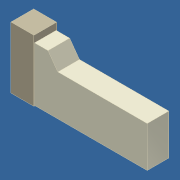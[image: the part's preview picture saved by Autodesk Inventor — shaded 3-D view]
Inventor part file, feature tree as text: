
AUTODESK INVENTOR PART (.ipt)
format: ipt  version: unknown  size: 201,216 bytes
history: native  units: in
note: dims shown in document units (in); Inventor stores cm internally (conversion verified against a paired STEP export)
features: extrude x4, sketch x4
ambient origin geometry x8: Origin, YZ Plane, XZ Plane, XY Plane, X Axis, Y Axis, Z Axis, Center Point
bodies: Solid1 (feature_tree)
feature tree (8):
  extrude  "Extrusion1"  Depth=0.425in
  extrude  "Extrusion2"  Depth=0.75in
  extrude  "Extrusion3"  Depth=0.25in
  extrude  "Extrusion4"  Depth=0.01in TaperAngle=0.0deg
  sketch  "Sketch1"  dims[d0=1.125in d1=0.425in]
  sketch  "Sketch2"  dims[d2=1.0in d3=0.75in]
  sketch  "Sketch3"  dims[d4=1.65in d5=0.25in]
  sketch  "Sketch4"  dims[d6=0.4in d7=0.0in d8=0.01in d9=0.0in d10=0.01in d11=0.0in d12=0.01in d13=0.0in]
